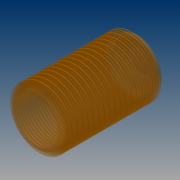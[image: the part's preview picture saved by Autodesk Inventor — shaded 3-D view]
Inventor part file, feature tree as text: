
AUTODESK INVENTOR PART (.ipt)
format: ipt  version: 2014 (Build 180170000, 170)  size: 458,752 bytes
history: native  units: mm
features: revolve x1, sketch x1
ambient origin geometry x8: Origin, YZ Plane, XZ Plane, XY Plane, X Axis, Y Axis, Z Axis, Center Point
bodies: Solid1 (feature_tree)
feature tree (2):
  revolve  "Revolution1"  [1 undecoded]
  sketch  "Sketch1"  dims[d34=40.0mm d36=20.0mm d37=10.0mm d38=5.0mm d39=10.0mm d40=2.0mm d41=10.0mm d42=10.0mm d43=2.0mm d44=10.0mm d45=2.0mm d46=10.0mm d47=2.0mm d48=10.0mm d49=2.0mm d50=10.0mm d51=2.0mm d52=10.0mm d53=2.0mm d54=10.0mm d55=2.0mm d56=10.0mm d57=2.0mm d59=2.0mm d62=3.0mm d63=3.0mm d64=3.0mm d65=3.0mm d66=3.0mm d67=3.0mm d68=3.0mm d69=3.0mm d70=3.0mm d72=90.0deg d73=2.0mm d74=2.0mm d75=2.0mm d76=2.0mm d77=2.0mm d78=2.0mm d79=2.0mm d80=2.0mm d81=3.0mm d82=10.0mm d83=3.0mm d84=3.0mm d85=3.0mm d86=3.0mm d87=3.0mm d88=3.0mm d89=3.0mm d90=195.0mm d91=2.0mm d92=2.0mm d93=2.0mm d94=2.0mm d95=2.0mm d96=2.0mm d97=2.0mm d98=2.0mm d99=2.0mm d101=3.0mm d102=3.0mm d103=3.0mm d104=3.0mm d105=3.0mm d106=3.0mm d107=3.0mm d108=3.0mm d109=3.0mm d110=2.0mm d111=2.0mm d112=2.0mm d113=3.0mm d114=3.0mm d115=3.0mm d116=2.0mm d117=2.0mm d118=2.0mm d119=2.0mm d120=2.0mm d121=3.0mm d122=3.0mm d123=3.0mm d124=3.0mm d125=3.0mm]
note: 1 required parameter value undecoded (feature->parameter linkage not recoverable at this tier; creation-order binding heuristic only, values carry confidence <= 0.55)
